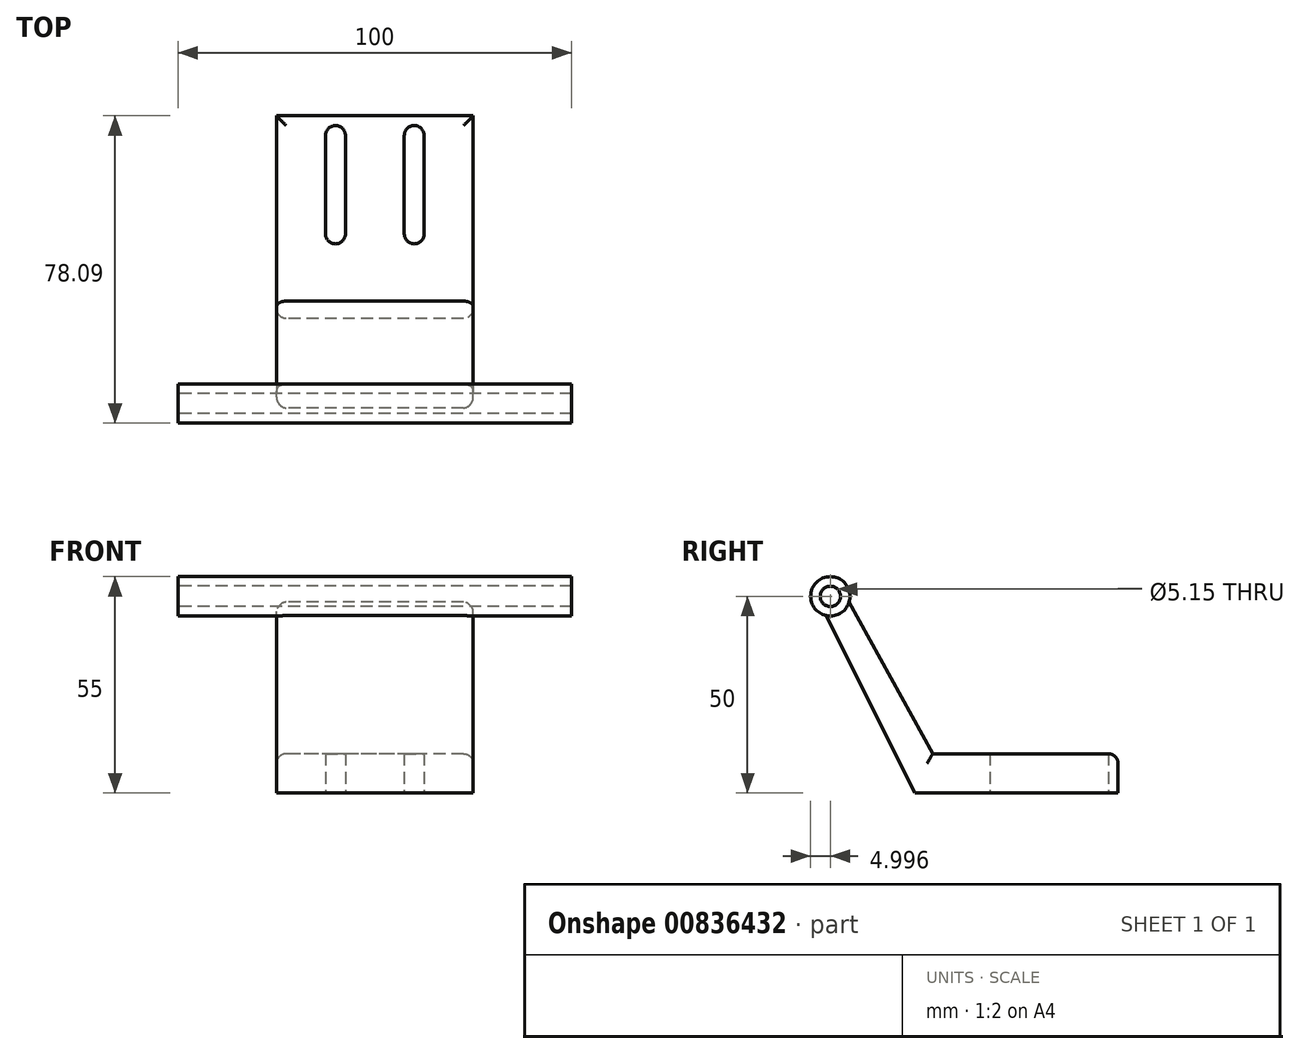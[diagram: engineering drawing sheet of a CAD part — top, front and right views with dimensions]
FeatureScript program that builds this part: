
annotation { "Feature Type Name" : "Feature", "Feature Type Description" : "" }
export const myFeature = defineFeature(function(context is Context, id is Id, definition is map)
    precondition{}
    {
        {
            var Q0;
            Q0=qCreatedBy(makeId("Right.planeOp"),FACE);
            var sketch = newSketch(context, id + "F0", { "sketchPlane" : qUnion([Q0])});
            skLineSegment(sketch, "E0", {"start": v(0, 0) * mm, "end": v(0, 10) * mm});
            skCircle(sketch, "E1", {"center": v(-73.1, 50) * mm, "radius": 5 * mm});
            skCircle(sketch, "E2", {"center": v(-73.1, 50) * mm, "radius": 2.58 * mm});
            skLineSegment(sketch, "E3", {"start": v(-47.08, 10) * mm, "end": v(-68.31, 48.54) * mm});
            skLineSegment(sketch, "E4", {"start": v(-51.54, 0) * mm, "end": v(-74.22, 45.13) * mm});
            skLineSegment(sketch, "E5", {"start": v(0, 0) * mm, "end": v(-51.54, 0) * mm});
            skLineSegment(sketch, "E6", {"start": v(0, 10) * mm, "end": v(-47.08, 10) * mm});
            skSolve(sketch);
        }
        {
            var Q0;
            Q0=makeQuery(id+"F0.imprint","IMPRINT",FACE,{"disambiguationData":[TD([[makeQuery(id+"F0.imprint","IMPRINT",EDGE,{"derivedFrom":sQuery(id+"F0.wireOp",EDGE,"E2")}),-1.0]])]});
            extrude(context, id + "F1", {"entities" : qUnion([Q0]), "endBound" : BoundingType.SYMMETRIC, "depth" : 100 * mm, "offsetDistance" : 25 * mm});
        }
        {
            var Q0;
            Q0=makeQuery(id+"F0.imprint","IMPRINT",FACE,{"disambiguationData":[TD([[makeQuery(id+"F0.imprint","IMPRINT",EDGE,{"derivedFrom":sQuery(id+"F0.wireOp",EDGE,"E0")}),1.0]])]});
            extrude(context, id + "F2", {"entities" : qUnion([Q0]), "operationType" : NewBodyOperationType.ADD, "endBound" : BoundingType.SYMMETRIC, "depth" : 50 * mm, "offsetDistance" : 25 * mm});
        }
        {
            var Q0;
            Q0=qCreatedBy(makeId("Top.planeOp"),FACE);
            var sketch = newSketch(context, id + "F3", { "sketchPlane" : qUnion([Q0])});
            skLineSegment(sketch, "E7", {"start": v(-12.53, -5) * mm, "end": v(-12.53, -30) * mm});
            skLineSegment(sketch, "E8", {"start": v(7.47, -5) * mm, "end": v(7.47, -30) * mm});
            skLineSegment(sketch, "E9", {"start": v(7.48, -30) * mm, "end": v(12.53, -30) * mm});
            skLineSegment(sketch, "E10", {"start": v(7.47, -5) * mm, "end": v(12.52, -5) * mm});
            skLineSegment(sketch, "E11", {"start": v(12.52, -5) * mm, "end": v(12.52, -30) * mm});
            skLineSegment(sketch, "E12", {"start": v(-12.53, -30) * mm, "end": v(-7.48, -30) * mm});
            skLineSegment(sketch, "E13", {"start": v(-12.53, -5) * mm, "end": v(-7.48, -5) * mm});
            skLineSegment(sketch, "E14", {"start": v(-7.48, -30) * mm, "end": v(-7.48, -5) * mm});
            skCircle(sketch, "E15", {"center": v(-10, -5) * mm, "radius": 2.52 * mm});
            skCircle(sketch, "E16", {"center": v(-10, -30) * mm, "radius": 2.52 * mm});
            skCircle(sketch, "E17", {"center": v(10, -5) * mm, "radius": 2.52 * mm});
            skCircle(sketch, "E18", {"center": v(10, -30) * mm, "radius": 2.53 * mm});
            skSolve(sketch);
        }
        {
            var Q0;
            Q0=qSketchRegion(id+"F3",true);
            extrude(context, id + "F4", {"entities" : qUnion([Q0]), "operationType" : NewBodyOperationType.REMOVE, "depth" : 10 * mm, "offsetDistance" : 25 * mm});
        }
        {
            var Q0;
            Q0=makeQuery(id+"F2.opExtrude","CAP_EDGE",EDGE,{"disambiguationData":[OSD([sQuery(id+"F0.wireOp",EDGE,"E6")])],"isStart":true});
            var Q1;
            Q1=makeQuery(id+"F2.opExtrude","CAP_EDGE",EDGE,{"disambiguationData":[OSD([sQuery(id+"F0.wireOp",EDGE,"E3")])],"isStart":true});
            var Q2;
            Q2=makeQuery(id+"F2.opExtrude","CAP_EDGE",EDGE,{"disambiguationData":[OSD([sQuery(id+"F0.wireOp",EDGE,"E4")])],"isStart":true});
            var Q3;
            Q3=makeQuery(id+"F2.opExtrude","SWEPT_EDGE",EDGE,{"disambiguationData":[OSD([sQuery(id+"F0.wireOp",EDGE,"E0"),sQuery(id+"F0.wireOp",EDGE,"E6")])]});
            var Q4;
            Q4=makeQuery(id+"F2.opExtrude","CAP_EDGE",EDGE,{"disambiguationData":[OSD([sQuery(id+"F0.wireOp",EDGE,"E6")])],"isStart":false});
            var Q5;
            Q5=makeQuery(id+"F2.opExtrude","CAP_EDGE",EDGE,{"disambiguationData":[OSD([sQuery(id+"F0.wireOp",EDGE,"E3")])],"isStart":false});
            var Q6;
            Q6=makeQuery(id+"F2.opExtrude","CAP_EDGE",EDGE,{"disambiguationData":[OSD([sQuery(id+"F0.wireOp",EDGE,"E4")])],"isStart":false});
            fillet(context, id + "F5", {"entities" : qUnion([Q0, Q1, Q2, Q3, Q4, Q5, Q6]), "radius" : 2.5 * mm, "tangentPropagation" : true, "allowEdgeOverflow" : false});
        }
    });
